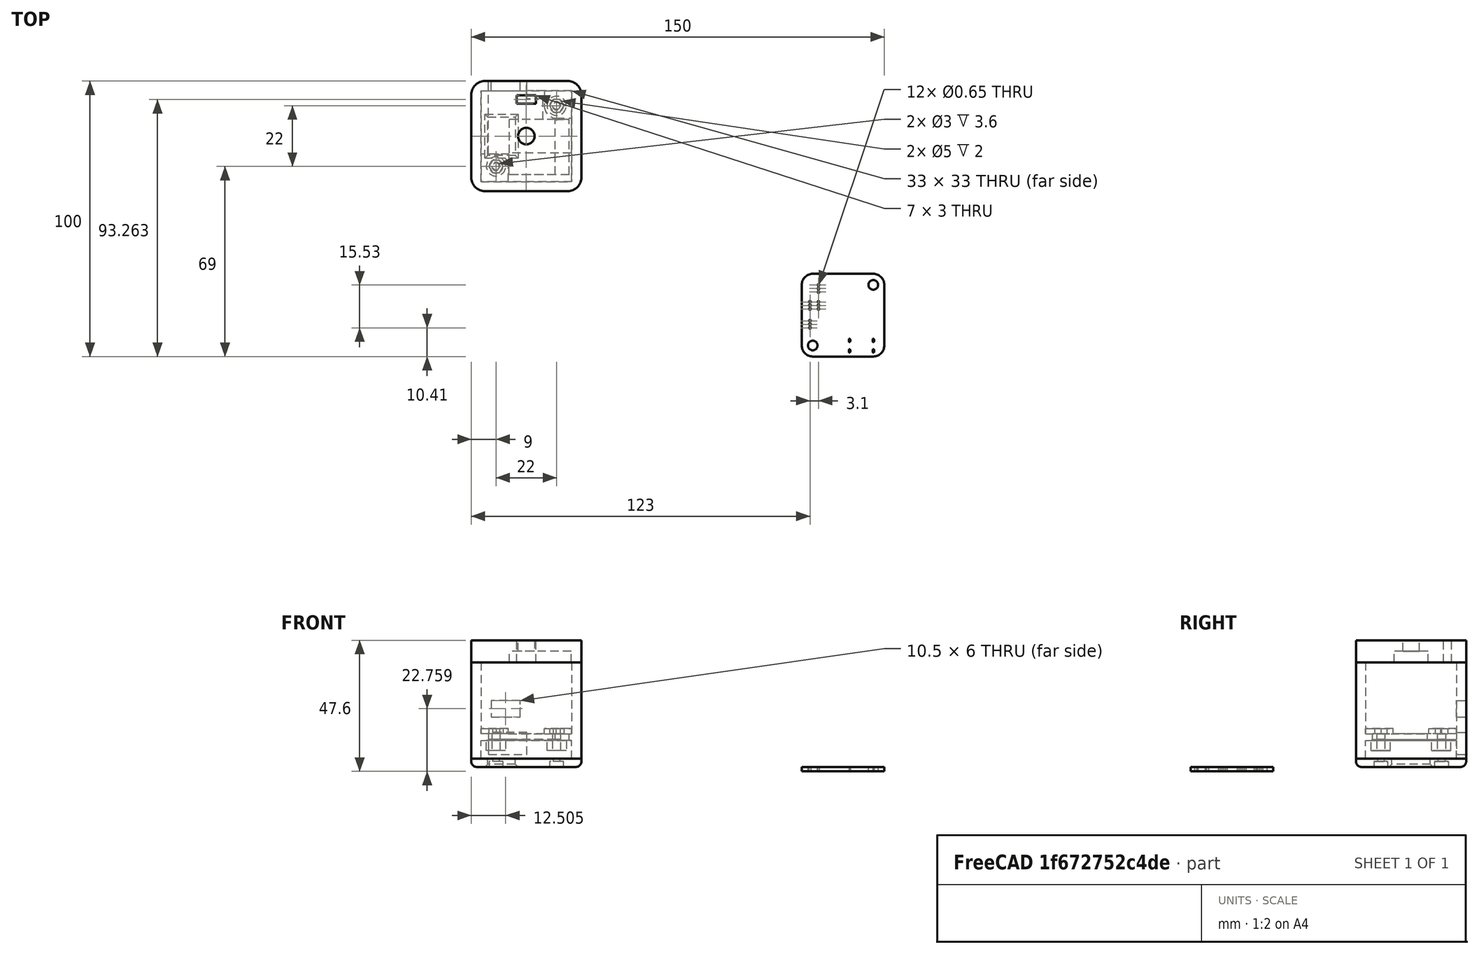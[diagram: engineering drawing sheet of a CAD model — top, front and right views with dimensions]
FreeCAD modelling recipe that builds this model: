
FCSTD DOCUMENT  (FreeCAD 1.0R39319 (Git))
Label: model
License: All rights reserved
LicenseURL: https://en.wikipedia.org/wiki/All_rights_reserved
objects: Sketcher::SketchObject×20, PartDesign::Pocket×13, PartDesign::Pad×6, PartDesign::Fillet×4, PartDesign::Body×3, App::Part×3, PartDesign::Chamfer×1, Mesh::Feature×1, PartDesign::CoordinateSystem×1, Part::Feature×1
note: 117 computed .brp shape members not serialized (recipe doc carries the construction recipe); baked Part::Feature solids carry a one-line shape summary decoded from their .brp

FEATURE [Sketcher::SketchObject] Sketch
  ArcFitTolerance = 1e-06
  AttachmentSupport = -> [XY_Plane]
  FullyConstrained = true
  MakeInternals = false
  MapMode = 5
  sketch-geometry (5):
    g0: LineSegment StartX=-20 StartY=-20 StartZ=0 EndX=20 EndY=-20 EndZ=0
    g1: LineSegment StartX=20 StartY=-20 StartZ=0 EndX=20 EndY=20 EndZ=0
    g2: LineSegment StartX=20 StartY=20 StartZ=0 EndX=-20 EndY=20 EndZ=0
    g3: LineSegment StartX=-20 StartY=20 StartZ=0 EndX=-20 EndY=-20 EndZ=0
    g4: GeomPoint [constr] X=0 Y=0 Z=0
  constraints (12):
    c: Coincident(g0,g1)
    c: Coincident(g1,g2)
    c: Coincident(g2,g3)
    c: Coincident(g3,g0)
    c: Horizontal(g0)
    c: Horizontal(g2)
    c: Vertical(g1)
    c: Vertical(g3)
    c: Symmetric(g2,g0,g4)
    c: Distance(g1,g3) = 40
    c: Distance(g0,g2) = 40
    c: Coincident(g4,g-1)
FEATURE [PartDesign::Pad] Pad
  Direction = (0,0,1)
  Length = 3
  Length2 = 10
  Profile = -> Sketch
  ReferenceAxis = -> Sketch [N_Axis]
  Refine = true
  Suppressed = false
  Type = 0
FEATURE [Sketcher::SketchObject] Sketch001
  ArcFitTolerance = 1e-06
  AttachmentSupport = -> [Pad]
  FullyConstrained = true
  MakeInternals = false
  MapMode = 5
  Placement = pos=(0,0,0) rot=(1,0,0;3.14159rad)
  sketch-geometry (2):
    g0: Circle CenterX=-11 CenterY=11 CenterZ=0 NormalX=0 NormalY=0 NormalZ=1 AngleXU=0 Radius=2.5
    g1: Circle CenterX=11 CenterY=-11 CenterZ=0 NormalX=0 NormalY=0 NormalZ=1 AngleXU=0 Radius=2.5
  constraints (6):
    c: Diameter(g0) = 5
    c: DistanceX(g0,g-1) = 11
    c: DistanceX(g0,g1) = 22
    c: Equal(g0,g1)
    c: DistanceY(g-1,g0) = 11
    c: DistanceY(g1,g0) = 22
FEATURE [PartDesign::Pocket] Pocket
  BaseFeature = -> Pad
  Direction = (0,0,1)
  Length = 2
  Length2 = 5
  Profile = -> Sketch001
  ReferenceAxis = -> Sketch001 [N_Axis]
  Refine = true
  Suppressed = false
  Type = 0
FEATURE [Sketcher::SketchObject] Sketch002
  ArcFitTolerance = 1e-06
  AttachmentSupport = -> [Pocket]
  ExternalGeometry = -> [Pocket]
  FullyConstrained = true
  MakeInternals = false
  MapMode = 5
  Placement = pos=(0,0,2) rot=(1,0,0;3.14159rad)
  sketch-geometry (2):
    g0: Circle CenterX=-11 CenterY=11 CenterZ=0 NormalX=0 NormalY=0 NormalZ=1 AngleXU=0 Radius=1.25
    g1: Circle CenterX=11 CenterY=-11 CenterZ=0 NormalX=0 NormalY=0 NormalZ=1 AngleXU=0 Radius=1.25
  constraints (4):
    c: Diameter(g0) = 2.5
    c: Coincident(g0,g-3)
    c: Diameter(g1) = 2.5
    c: Coincident(g1,g-4)
FEATURE [PartDesign::Pocket] Pocket001
  BaseFeature = -> Pocket
  Direction = (0,0,1)
  Length = 1
  Length2 = 5
  Profile = -> Sketch002
  ReferenceAxis = -> Sketch002 [N_Axis]
  Refine = true
  Suppressed = false
  Type = 0
FEATURE [PartDesign::Fillet] Fillet
  Base = -> Pocket001 [Edge1,Edge5,Edge8,Edge2]
  BaseFeature = -> Pocket001
  Radius = 5
  Refine = true
  SupportTransform = false
  Suppressed = false
  UseAllEdges = false
FEATURE [Sketcher::SketchObject] Sketch003
  ArcFitTolerance = 1e-06
  AttachmentSupport = -> [Fillet]
  ExternalGeometry = -> [Fillet]
  FullyConstrained = true
  MakeInternals = false
  MapMode = 5
  Placement = pos=(0,0,0) rot=(1,0,0;3.14159rad)
  sketch-geometry (9):
    g0: LineSegment StartX=-14 StartY=7 StartZ=0 EndX=-14 EndY=-7 EndZ=0
    g1: LineSegment StartX=-14 StartY=-7 StartZ=0 EndX=-4 EndY=-7 EndZ=0
    g2: LineSegment StartX=-4 StartY=-7 StartZ=0 EndX=-4 EndY=7 EndZ=0
    g3: LineSegment StartX=-4 StartY=7 StartZ=0 EndX=-14 EndY=7 EndZ=0
    g4: LineSegment [constr] StartX=-15 StartY=-15 StartZ=0 EndX=15 EndY=-15 EndZ=0
    g5: LineSegment [constr] StartX=15 StartY=-15 StartZ=0 EndX=15 EndY=15 EndZ=0
    g6: LineSegment [constr] StartX=15 StartY=15 StartZ=0 EndX=-15 EndY=15 EndZ=0
    g7: LineSegment [constr] StartX=-15 StartY=15 StartZ=0 EndX=-15 EndY=-15 EndZ=0
    g8: GeomPoint [constr] X=0 Y=0 Z=0
  constraints (24):
    c: Coincident(g0,g1)
    c: Coincident(g1,g2)
    c: Coincident(g2,g3)
    c: Coincident(g3,g0)
    c: Vertical(g0)
    c: Vertical(g2)
    c: Horizontal(g1)
    c: Horizontal(g3)
    c: Distance(g0,g2) = 10
    c: Distance(g1,g3) = 14
    c: Coincident(g4,g5)
    c: Coincident(g5,g6)
    c: Coincident(g6,g7)
    c: Coincident(g7,g4)
    c: Horizontal(g4)
    c: Horizontal(g6)
    c: Vertical(g5)
    c: Vertical(g7)
    c: Symmetric(g6,g4,g8)
    c: Distance(g5,g7) = 30
    c: Distance(g4,g6) = 30
    c: Coincident(g8,g-1)
    c: DistanceX(g4,g0) = 1
    c: DistanceY(g4,g0) = 8
FEATURE [PartDesign::Pocket] Pocket002
  BaseFeature = -> Fillet
  Direction = (0,0,1)
  Length = 3
  Length2 = 5
  Profile = -> Sketch003
  ReferenceAxis = -> Sketch003 [N_Axis]
  Refine = true
  Suppressed = false
  Type = 0
FEATURE [PartDesign::Chamfer] Chamfer
  Angle = 45
  Base = -> Pocket002 [Edge13,Edge16,Edge15,Edge14]
  BaseFeature = -> Pocket002
  ChamferType = 0
  FlipDirection = false
  Refine = true
  Size = 1
  Size2 = 1
  SupportTransform = false
  Suppressed = false
  UseAllEdges = false
FEATURE [Sketcher::SketchObject] Sketch004
  ArcFitTolerance = 1e-06
  AttachmentSupport = -> [XY_Plane001]
  FullyConstrained = true
  MakeInternals = false
  MapMode = 5
  sketch-geometry (5):
    g0: LineSegment StartX=-20 StartY=-20 StartZ=0 EndX=20 EndY=-20 EndZ=0
    g1: LineSegment StartX=20 StartY=-20 StartZ=0 EndX=20 EndY=20 EndZ=0
    g2: LineSegment StartX=20 StartY=20 StartZ=0 EndX=-20 EndY=20 EndZ=0
    g3: LineSegment StartX=-20 StartY=20 StartZ=0 EndX=-20 EndY=-20 EndZ=0
    g4: GeomPoint [constr] X=0 Y=0 Z=0
  constraints (12):
    c: Coincident(g0,g1)
    c: Coincident(g1,g2)
    c: Coincident(g2,g3)
    c: Coincident(g3,g0)
    c: Horizontal(g0)
    c: Horizontal(g2)
    c: Vertical(g1)
    c: Vertical(g3)
    c: Symmetric(g2,g0,g4)
    c: Distance(g1,g3) = 40
    c: Distance(g0,g2) = 40
    c: Coincident(g4,g-1)
FEATURE [PartDesign::Pad] Pad001  label="box"
  Direction = (0,0,1)
  Length = 35
  Length2 = 10
  Profile = -> Sketch004
  ReferenceAxis = -> Sketch004 [N_Axis]
  Refine = true
  Suppressed = false
  Type = 0
FEATURE [PartDesign::Fillet] Fillet001  label="rounded box"
  Base = -> Pad001 [Edge1,Edge2,Edge5,Edge8]
  BaseFeature = -> Pad001
  Radius = 5
  Refine = true
  SupportTransform = false
  Suppressed = false
  UseAllEdges = false
FEATURE [Sketcher::SketchObject] Sketch005
  ArcFitTolerance = 1e-06
  AttachmentSupport = -> [Fillet001]
  FullyConstrained = true
  MakeInternals = false
  MapMode = 5
  Placement = pos=(0,0,0) rot=(1,0,0;3.14159rad)
  sketch-geometry (5):
    g0: LineSegment StartX=-16.5 StartY=-16.5 StartZ=0 EndX=16.5 EndY=-16.5 EndZ=0
    g1: LineSegment StartX=16.5 StartY=-16.5 StartZ=0 EndX=16.5 EndY=16.5 EndZ=0
    g2: LineSegment StartX=16.5 StartY=16.5 StartZ=0 EndX=-16.5 EndY=16.5 EndZ=0
    g3: LineSegment StartX=-16.5 StartY=16.5 StartZ=0 EndX=-16.5 EndY=-16.5 EndZ=0
    g4: GeomPoint [constr] X=0 Y=0 Z=0
  constraints (12):
    c: Coincident(g0,g1)
    c: Coincident(g1,g2)
    c: Coincident(g2,g3)
    c: Coincident(g3,g0)
    c: Horizontal(g0)
    c: Horizontal(g2)
    c: Vertical(g1)
    c: Vertical(g3)
    c: Symmetric(g2,g0,g4)
    c: Distance(g1,g3) = 33
    c: Distance(g0,g2) = 33
    c: Coincident(g4,g-1)
FEATURE [PartDesign::Pocket] Pocket003  label="bottom hole"
  BaseFeature = -> Fillet001
  Direction = (0,0,1)
  Length = 7
  Length2 = 5
  Profile = -> Sketch005
  ReferenceAxis = -> Sketch005 [N_Axis]
  Refine = true
  Suppressed = false
  Type = 0
FEATURE [Sketcher::SketchObject] Sketch006
  ArcFitTolerance = 1e-06
  AttachmentSupport = -> [Pocket003]
  ExternalGeometry = -> [Pocket003]
  FullyConstrained = true
  MakeInternals = false
  MapMode = 5
  Placement = pos=(0,0,7) rot=(1,0,0;3.14159rad)
  sketch-geometry (4):
    g0: LineSegment StartX=15.5 StartY=14 StartZ=0 EndX=10.5 EndY=14 EndZ=0
    g1: LineSegment StartX=10.5 StartY=14 StartZ=0 EndX=10.5 EndY=-6 EndZ=0
    g2: LineSegment StartX=10.5 StartY=-6 StartZ=0 EndX=15.5 EndY=-6 EndZ=0
    g3: LineSegment StartX=15.5 StartY=-6 StartZ=0 EndX=15.5 EndY=14 EndZ=0
  constraints (12):
    c: Coincident(g0,g1)
    c: Coincident(g1,g2)
    c: Coincident(g2,g3)
    c: Coincident(g3,g0)
    c: Horizontal(g0)
    c: Horizontal(g2)
    c: Vertical(g1)
    c: Vertical(g3)
    c: Distance(g1,g3) = 5
    c: Distance(g0,g2) = 20
    c: DistanceX(g0,g-3) = 1
    c: DistanceY(g0,g-3) = 2.5
FEATURE [PartDesign::Pocket] Pocket004  label="cable hole"
  BaseFeature = -> Pocket003
  Direction = (0,0,1)
  Length = 2
  Length2 = 5
  Profile = -> Sketch006
  ReferenceAxis = -> Sketch006 [N_Axis]
  Refine = true
  Suppressed = false
  Type = 0
FEATURE [Sketcher::SketchObject] Sketch007
  ArcFitTolerance = 1e-06
  AttachmentSupport = -> [Pocket004]
  FullyConstrained = true
  MakeInternals = false
  MapMode = 5
  Placement = pos=(0,0,7) rot=(1,0,0;3.14159rad)
  sketch-geometry (2):
    g0: Circle CenterX=-11 CenterY=11 CenterZ=0 NormalX=0 NormalY=0 NormalZ=1 AngleXU=0 Radius=3.5
    g1: Circle CenterX=11 CenterY=-11 CenterZ=0 NormalX=0 NormalY=0 NormalZ=1 AngleXU=0 Radius=3.5
  constraints (6):
    c: Diameter(g0) = 7
    c: Diameter(g1) = 7
    c: DistanceX(g0,g1) = 22
    c: DistanceY(g1,g0) = 22
    c: DistanceY(g-1,g0) = 11
    c: DistanceX(g0,g-1) = 11
FEATURE [PartDesign::Pad] Pad002  label="standoffs"
  BaseFeature = -> Pocket004
  Direction = (0,0,-1)
  Length = 4
  Length2 = 10
  Profile = -> Sketch007
  ReferenceAxis = -> Sketch007 [N_Axis]
  Refine = true
  Suppressed = false
  Type = 0
FEATURE [Sketcher::SketchObject] Sketch009
  ArcFitTolerance = 1e-06
  FullyConstrained = true
  MakeInternals = false
  MapMode = 5
  Placement = pos=(0,0,40) rot=(0,0,1;0rad)
  sketch-geometry (5):
    g0: LineSegment StartX=-16.5 StartY=-16.5 StartZ=0 EndX=16.5 EndY=-16.5 EndZ=0
    g1: LineSegment StartX=16.5 StartY=-16.5 StartZ=0 EndX=16.5 EndY=16.5 EndZ=0
    g2: LineSegment StartX=16.5 StartY=16.5 StartZ=0 EndX=-16.5 EndY=16.5 EndZ=0
    g3: LineSegment StartX=-16.5 StartY=16.5 StartZ=0 EndX=-16.5 EndY=-16.5 EndZ=0
    g4: GeomPoint [constr] X=0 Y=0 Z=0
  constraints (12):
    c: Coincident(g0,g1)
    c: Coincident(g1,g2)
    c: Coincident(g2,g3)
    c: Coincident(g3,g0)
    c: Horizontal(g0)
    c: Horizontal(g2)
    c: Vertical(g1)
    c: Vertical(g3)
    c: Symmetric(g2,g0,g4)
    c: Distance(g1,g3) = 33
    c: Distance(g0,g2) = 33
    c: Coincident(g4,g-1)
FEATURE [PartDesign::Pocket] Pocket006  label="top hole"
  BaseFeature = -> Pad002
  Direction = (0,0,-1)
  Length = 31
  Length2 = 5
  Profile = -> Sketch009
  ReferenceAxis = -> Sketch009 [N_Axis]
  Refine = true
  Suppressed = false
  Type = 0
FEATURE [Sketcher::SketchObject] Sketch010
  ArcFitTolerance = 1e-06
  AttachmentSupport = -> [Pocket006]
  ExternalGeometry = -> [Pocket006]
  FullyConstrained = true
  MakeInternals = false
  MapMode = 5
  Placement = pos=(0,16.5,0) rot=(1,0,0;1.5708rad)
  sketch-geometry (4):
    g0: LineSegment StartX=-13.75 StartY=9.5 StartZ=0 EndX=-13.75 EndY=1.5 EndZ=0
    g1: LineSegment StartX=-13.75 StartY=1.5 StartZ=0 EndX=0.25 EndY=1.5 EndZ=0
    g2: LineSegment StartX=0.25 StartY=1.5 StartZ=0 EndX=0.25 EndY=9.5 EndZ=0
    g3: LineSegment StartX=0.25 StartY=9.5 StartZ=0 EndX=-13.75 EndY=9.5 EndZ=0
  constraints (12):
    c: Coincident(g0,g1)
    c: Coincident(g1,g2)
    c: Coincident(g2,g3)
    c: Coincident(g3,g0)
    c: Vertical(g0)
    c: Vertical(g2)
    c: Horizontal(g1)
    c: Horizontal(g3)
    c: DistanceX(g-3,g0) = 2.75
    c: DistanceX(g3,g3) = 14
    c: DistanceY(g0,g0) = 8
    c: DistanceY(g-3,g0) = 1.5
FEATURE [PartDesign::Pocket] Pocket007  label="usb hole"
  BaseFeature = -> Pocket006
  Direction = (0,1,-2e-16)
  Length = 4
  Length2 = 5
  Profile = -> Sketch010
  ReferenceAxis = -> Sketch010 [N_Axis]
  Refine = true
  Suppressed = false
  Type = 0
FEATURE [Sketcher::SketchObject] Sketch011
  ArcFitTolerance = 1e-06
  AttachmentSupport = -> [Pocket007]
  FullyConstrained = false
  MakeInternals = false
  MapMode = 5
  Placement = pos=(0,16.5,0) rot=(1,0,0;1.5708rad)
  sketch-geometry (4):
    g0: LineSegment StartX=-2.24469 StartY=15.159 StartZ=0 EndX=-2.24469 EndY=21.159 EndZ=0
    g1: LineSegment StartX=-2.24469 StartY=21.159 StartZ=0 EndX=-12.7447 EndY=21.159 EndZ=0
    g2: LineSegment StartX=-12.7447 StartY=21.159 StartZ=0 EndX=-12.7447 EndY=15.159 EndZ=0
    g3: LineSegment StartX=-12.7447 StartY=15.159 StartZ=0 EndX=-2.24469 EndY=15.159 EndZ=0
  constraints (10):
    c: Coincident(g0,g1)
    c: Coincident(g1,g2)
    c: Coincident(g2,g3)
    c: Coincident(g3,g0)
    c: Vertical(g0)
    c: Vertical(g2)
    c: Horizontal(g1)
    c: Horizontal(g3)
    c: DistanceX(g1,g1) = 10.5
    c: DistanceY(g2,g2) = 6
FEATURE [PartDesign::Pocket] Pocket008  label="dmx hole"
  BaseFeature = -> Pocket007
  Direction = (0,1,-2e-16)
  Length = 4
  Length2 = 5
  Profile = -> Sketch011
  ReferenceAxis = -> Sketch011 [N_Axis]
  Refine = true
  Suppressed = false
  Type = 0
FEATURE [Sketcher::SketchObject] Sketch012
  ArcFitTolerance = 1e-06
  AttachmentSupport = -> [Pocket008]
  ExternalGeometry = -> [Pocket008]
  FullyConstrained = false
  MakeInternals = false
  MapMode = 5
  Placement = pos=(0,0,9) rot=(0,0,1;0rad)
  sketch-geometry (10):
    g0: LineSegment StartX=16.5 StartY=16.5 StartZ=0 EndX=6.5 EndY=16.5 EndZ=0
    g1: LineSegment StartX=6.5 StartY=16.5 StartZ=0 EndX=6.5 EndY=10.8083 EndZ=0
    g2: LineSegment StartX=10.8083 StartY=6.5 StartZ=0 EndX=16.5 EndY=6.5 EndZ=0
    g3: LineSegment StartX=16.5 StartY=6.5 StartZ=0 EndX=16.5 EndY=16.5 EndZ=0
    g4: LineSegment StartX=-16.5 StartY=-16.5 StartZ=0 EndX=-6.5 EndY=-16.5 EndZ=0
    g5: LineSegment StartX=-6.5 StartY=-16.5 StartZ=0 EndX=-6.5 EndY=-10.8083 EndZ=0
    g6: LineSegment StartX=-10.8083 StartY=-6.5 StartZ=0 EndX=-16.5 EndY=-6.5 EndZ=0
    g7: LineSegment StartX=-16.5 StartY=-6.5 StartZ=0 EndX=-16.5 EndY=-16.5 EndZ=0
    g8: ArcOfCircle CenterX=11 CenterY=11 CenterZ=0 NormalX=0 NormalY=0 NormalZ=1 AngleXU=0 Radius=4.50408 StartAngle=3.18416 EndAngle=4.66982
    g9: ArcOfCircle CenterX=-11 CenterY=-11 CenterZ=0 NormalX=0 NormalY=0 NormalZ=1 AngleXU=0 Radius=4.50408 StartAngle=0.0425652 EndAngle=1.52823
  constraints (27):
    c: Coincident(g0,g1)
    c: Coincident(g2,g3)
    c: Coincident(g3,g0)
    c: Horizontal(g0)
    c: Horizontal(g2)
    c: Vertical(g1)
    c: Vertical(g3)
    c: Coincident(g0,g-8)
    c: Coincident(g4,g5)
    c: Coincident(g6,g7)
    c: Coincident(g7,g4)
    c: Horizontal(g4)
    c: Horizontal(g6)
    c: Vertical(g5)
    c: Vertical(g7)
    c: Coincident(g4,g-7)
    c: Equal(g4,g7)
    c: Equal(g7,g0)
    c: Equal(g0,g3)
    c: Equal(g5,g2)
    c: Coincident(g8,g-4)
    c: Coincident(g8,g2)
    c: Coincident(g8,g1)
    c: Coincident(g9,g-3)
    c: Coincident(g9,g6)
    c: Coincident(g9,g5)
    c: DistanceY(g3,g3) = 10
FEATURE [PartDesign::Pad] Pad003
  BaseFeature = -> Pocket008
  Direction = (0,0,1)
  Length = 2
  Length2 = 10
  Profile = -> Sketch012
  ReferenceAxis = -> Sketch012 [N_Axis]
  Refine = true
  Suppressed = false
  Type = 0
FEATURE [Sketcher::SketchObject] Sketch013
  ArcFitTolerance = 1e-06
  AttachmentSupport = -> [Pad003]
  ExternalGeometry = -> [Pad003]
  FullyConstrained = true
  MakeInternals = false
  MapMode = 5
  Placement = pos=(0,0,3) rot=(1,0,0;3.14159rad)
  sketch-geometry (2):
    g0: Circle CenterX=-11 CenterY=11 CenterZ=0 NormalX=0 NormalY=0 NormalZ=1 AngleXU=0 Radius=1.5
    g1: Circle CenterX=11 CenterY=-11 CenterZ=0 NormalX=0 NormalY=0 NormalZ=1 AngleXU=0 Radius=1.5
  constraints (4):
    c: Diameter(g0) = 3
    c: Coincident(g0,g-4)
    c: Diameter(g1) = 3
    c: Coincident(g1,g-3)
FEATURE [PartDesign::Pocket] Pocket009
  BaseFeature = -> Pad003
  Direction = (0,0,1)
  Length = 8
  Length2 = 5
  Profile = -> Sketch013
  ReferenceAxis = -> Sketch013 [N_Axis]
  Refine = true
  Suppressed = false
  Type = 0
FEATURE [Sketcher::SketchObject] Sketch014
  ArcFitTolerance = 1e-06
  AttachmentSupport = -> [Pocket009]
  ExternalGeometry = -> [Pocket009]
  FullyConstrained = true
  MakeInternals = false
  MapMode = 5
  Placement = pos=(0,0,11) rot=(0,0,1;0rad)
  sketch-geometry (14):
    g0: LineSegment StartX=13.6 StartY=11 StartZ=0 EndX=12.3 EndY=13.2517 EndZ=0
    g1: LineSegment StartX=12.3 StartY=13.2517 StartZ=0 EndX=9.7 EndY=13.2517 EndZ=0
    g2: LineSegment StartX=9.7 StartY=13.2517 StartZ=0 EndX=8.4 EndY=11 EndZ=0
    g3: LineSegment StartX=8.4 StartY=11 StartZ=0 EndX=9.7 EndY=8.74833 EndZ=0
    g4: LineSegment StartX=9.7 StartY=8.74833 StartZ=0 EndX=12.3 EndY=8.74833 EndZ=0
    g5: LineSegment StartX=12.3 StartY=8.74833 StartZ=0 EndX=13.6 EndY=11 EndZ=0
    g6: Circle [constr] CenterX=11 CenterY=11 CenterZ=0 NormalX=0 NormalY=0 NormalZ=1 AngleXU=0 Radius=2.6
    g7: LineSegment StartX=-8.4 StartY=-11 StartZ=0 EndX=-9.7 EndY=-8.74833 EndZ=0
    g8: LineSegment StartX=-9.7 StartY=-8.74833 StartZ=0 EndX=-12.3 EndY=-8.74833 EndZ=0
    g9: LineSegment StartX=-12.3 StartY=-8.74833 StartZ=0 EndX=-13.6 EndY=-11 EndZ=0
    g10: LineSegment StartX=-13.6 StartY=-11 StartZ=0 EndX=-12.3 EndY=-13.2517 EndZ=0
    g11: LineSegment StartX=-12.3 StartY=-13.2517 StartZ=0 EndX=-9.7 EndY=-13.2517 EndZ=0
    g12: LineSegment StartX=-9.7 StartY=-13.2517 StartZ=0 EndX=-8.4 EndY=-11 EndZ=0
    g13: Circle [constr] CenterX=-11 CenterY=-11 CenterZ=0 NormalX=0 NormalY=0 NormalZ=1 AngleXU=0 Radius=2.6
  constraints (32):
    c: Coincident(g0,g1)
    c: Coincident(g1,g2)
    c: Coincident(g2,g3)
    c: Coincident(g3,g4)
    c: Coincident(g4,g5)
    c: Coincident(g5,g0)
    c: Equal(g0, g1-g5) x5
    c: PointOnObject(g0,g6)
    c: PointOnObject(g1,g6)
    c: PointOnObject(g2,g6)
    c: PointOnObject(g3,g6)
    c: PointOnObject(g4,g6)
    c: PointOnObject(g5,g6)
    c: Radius(g6) = 2.6
    c: Coincident(g6,g-3)
    c: Coincident(g7,g8)
    c: Coincident(g8,g9)
    c: Coincident(g9,g10)
    c: Coincident(g10,g11)
    c: Coincident(g11,g12)
    c: Coincident(g12,g7)
    c: Equal(g7, g8-g12) x5
    c: PointOnObject(g7,g13)
    c: PointOnObject(g8,g13)
    c: PointOnObject(g9,g13)
    c: PointOnObject(g10,g13)
    c: PointOnObject(g11,g13)
    c: PointOnObject(g12,g13)
    c: Radius(g13) = 2.6
    c: Coincident(g13,g-4)
    c: Horizontal(g8)
    c: Horizontal(g1)
FEATURE [PartDesign::Pocket] Pocket010
  BaseFeature = -> Pocket009
  Direction = (0,0,-1)
  Length = 2
  Length2 = 5
  Profile = -> Sketch014
  ReferenceAxis = -> Sketch014 [N_Axis]
  Refine = true
  Suppressed = false
  Type = 0
FEATURE [PartDesign::Fillet] Fillet002
  Base = -> Chamfer [Edge6,Edge8,Edge5,Edge7,Edge9,Edge11,Edge12,Edge10]
  BaseFeature = -> Chamfer
  Radius = 2
  Refine = true
  SupportTransform = false
  Suppressed = false
  UseAllEdges = false
FEATURE [PartDesign::Body] Body  label="bottom cover"
  AllowCompound = false
  Group = -> [Sketch,Pad,Sketch001,Pocket,Sketch002,Pocket001,Fillet,Sketch003,Pocket002,Chamfer,Fillet002]
  Origin = -> Origin
  Tip = -> Fillet002
FEATURE [Sketcher::SketchObject] Sketch015
  ArcFitTolerance = 1e-06
  AttachmentSupport = -> [Pocket010]
  ExternalGeometry = -> [Pocket010]
  FullyConstrained = true
  MakeInternals = false
  MapMode = 5
  Placement = pos=(0,0,7) rot=(1,0,0;3.14159rad)
  sketch-geometry (14):
    g0: LineSegment StartX=-16.5 StartY=16.5 StartZ=0 EndX=16.5 EndY=16.5 EndZ=0
    g1: LineSegment StartX=16.5 StartY=16.5 StartZ=0 EndX=16.5 EndY=-16.5 EndZ=0
    g2: LineSegment StartX=16.5 StartY=-16.5 StartZ=0 EndX=0.25 EndY=-16.5 EndZ=0
    g3: LineSegment StartX=-16.5 StartY=16.5 StartZ=0 EndX=-16.5 EndY=-16.5 EndZ=0
    g4: LineSegment StartX=-16.5 StartY=-16.5 StartZ=0 EndX=-13.75 EndY=-16.5 EndZ=0
    g5: LineSegment StartX=15.5 StartY=14 StartZ=0 EndX=15.5 EndY=-6 EndZ=0
    g6: LineSegment StartX=15.5 StartY=-6 StartZ=0 EndX=6 EndY=-6 EndZ=0
    g7: LineSegment StartX=15.5 StartY=14 StartZ=0 EndX=-6.25 EndY=14 EndZ=0
    g8: LineSegment StartX=-6.25 StartY=14 StartZ=0 EndX=-6.25 EndY=6.5 EndZ=0
    g9: LineSegment StartX=-6.25 StartY=6.5 StartZ=0 EndX=-13.75 EndY=6.5 EndZ=0
    g10: LineSegment StartX=-13.75 StartY=6.5 StartZ=0 EndX=-13.75 EndY=-16.5 EndZ=0
    g11: LineSegment StartX=6 StartY=-6 StartZ=0 EndX=6 EndY=-13.5 EndZ=0
    g12: LineSegment StartX=6 StartY=-13.5 StartZ=0 EndX=0.25 EndY=-13.5 EndZ=0
    g13: LineSegment StartX=0.25 StartY=-13.5 StartZ=0 EndX=0.25 EndY=-16.5 EndZ=0
  constraints (34):
    c: Coincident(g0,g-5)
    c: Coincident(g0,g-5)
    c: Coincident(g1,g0)
    c: Coincident(g1,g-3)
    c: Coincident(g2,g1)
    c: Coincident(g2,g-3)
    c: Coincident(g3,g0)
    c: Coincident(g3,g-4)
    c: Coincident(g4,g3)
    c: Coincident(g4,g-6)
    c: Coincident(g6,g5)
    c: Horizontal(g6)
    c: Coincident(g5,g-7)
    c: Coincident(g7,g5)
    c: Horizontal(g7)
    c: Coincident(g8,g7)
    c: Vertical(g8)
    c: Coincident(g9,g8)
    c: Horizontal(g9)
    c: Coincident(g10,g9)
    c: Coincident(g10,g4)
    c: Vertical(g10)
    c: DistanceY(g8,g8) = 7.5
    c: DistanceX(g9,g9) = 7.5
    c: Coincident(g5,g-7)
    c: DistanceX(g6,g6) = 9.5
    c: Coincident(g11,g6)
    c: Vertical(g11)
    c: Coincident(g12,g11)
    c: Horizontal(g12)
    c: Coincident(g13,g12)
    c: Coincident(g13,g2)
    c: Vertical(g13)
    c: DistanceY(g11,g11) = 7.5
FEATURE [PartDesign::Pad] Pad004
  BaseFeature = -> Pocket010
  Direction = (0,0,-1)
  Length = 0.4
  Length2 = 10
  Profile = -> Sketch015
  ReferenceAxis = -> Sketch015 [N_Axis]
  Refine = true
  Suppressed = false
  Type = 0
FEATURE [PartDesign::Body] Body001  label="base"
  AllowCompound = false
  Group = -> [Sketch004,Pad001,Fillet001,Sketch005,Pocket003,Sketch006,Pocket004,Sketch007,Pad002,Sketch009,Pocket006,Sketch010,Pocket007,Sketch011,Pocket008,Sketch012,Pad003,Sketch013,Pocket009,Sketch014,Pocket010,Sketch015,Pad004]
  Origin = -> Origin001
  Placement = pos=(0,0,3) rot=(0,0,1;0rad)
  Tip = -> Pad004
FEATURE [Mesh::Feature] _g_servo  label="9g_servo"
  Placement = pos=(5,6,30) rot=(1,0,0;1.5708rad)
FEATURE [PartDesign::CoordinateSystem] Local_CS_8e13
  AttacherType = Attacher::AttachEngine3D
  MapMode = 2
  Placement = pos=(115,-65,0) rot=(0,0,1;0rad)
FEATURE [Sketcher::SketchObject] PCB_Sketch_8e13
  ArcFitTolerance = 1e-06
  FullyConstrained = false
  MakeInternals = false
  sketch-geometry (8):
    g0: LineSegment StartX=104 StartY=-50 StartZ=0 EndX=126 EndY=-50 EndZ=0
    g1: LineSegment StartX=100 StartY=-76 StartZ=0 EndX=100 EndY=-54 EndZ=0
    g2: LineSegment StartX=126 StartY=-80 StartZ=0 EndX=104 EndY=-80 EndZ=0
    g3: LineSegment StartX=130 StartY=-54 StartZ=0 EndX=130 EndY=-76 EndZ=0
    g4: ArcOfCircle CenterX=126 CenterY=-76 CenterZ=0 NormalX=0 NormalY=0 NormalZ=-1 AngleXU=-3.14159 Radius=4 StartAngle=0 EndAngle=1.5708
    g5: ArcOfCircle CenterX=104 CenterY=-76 CenterZ=0 NormalX=0 NormalY=0 NormalZ=-1 AngleXU=-1.5708 Radius=4 StartAngle=0 EndAngle=1.5708
    g6: ArcOfCircle CenterX=104 CenterY=-54 CenterZ=0 NormalX=0 NormalY=0 NormalZ=-1 AngleXU=1.06478e-07 Radius=4 StartAngle=0 EndAngle=1.5708
    g7: ArcOfCircle CenterX=126 CenterY=-54 CenterZ=0 NormalX=0 NormalY=0 NormalZ=-1 AngleXU=1.5708 Radius=4 StartAngle=0 EndAngle=1.5708
  constraints (8):
    c: Coincident(g1,g5)
    c: Coincident(g1,g6)
    c: Coincident(g2,g5)
    c: Coincident(g0,g6)
    c: Coincident(g2,g4)
    c: Coincident(g0,g7)
    c: Coincident(g3,g4)
    c: Coincident(g3,g7)
FEATURE [Part::Feature] Pcb_8e13
  shape: bbox 30 x 30 x 1.6 mm, 48 faces (baked)
FEATURE [App::Part] Board_Geoms_8e13
  Group = -> [Pcb_8e13,PCB_Sketch_8e13]
  Origin = -> Origin002
FEATURE [App::Part] Step_Models_8e13
  Origin = -> Origin004
FEATURE [App::Part] Board_8e13  label="desk-mh"
  Group = -> [Local_CS_8e13,Board_Geoms_8e13,Step_Models_8e13]
  Origin = -> Origin003
  Placement = pos=(115,-65,6) rot=(0,0,1;3.14159rad)
FEATURE [Sketcher::SketchObject] Sketch016
  ArcFitTolerance = 1e-06
  AttachmentSupport = -> [XY_Plane005]
  FullyConstrained = true
  MakeInternals = false
  MapMode = 5
  sketch-geometry (5):
    g0: LineSegment StartX=-20 StartY=-20 StartZ=0 EndX=20 EndY=-20 EndZ=0
    g1: LineSegment StartX=20 StartY=-20 StartZ=0 EndX=20 EndY=20 EndZ=0
    g2: LineSegment StartX=20 StartY=20 StartZ=0 EndX=-20 EndY=20 EndZ=0
    g3: LineSegment StartX=-20 StartY=20 StartZ=0 EndX=-20 EndY=-20 EndZ=0
    g4: GeomPoint [constr] X=0 Y=0 Z=0
  constraints (12):
    c: Coincident(g0,g1)
    c: Coincident(g1,g2)
    c: Coincident(g2,g3)
    c: Coincident(g3,g0)
    c: Horizontal(g0)
    c: Horizontal(g2)
    c: Vertical(g1)
    c: Vertical(g3)
    c: Symmetric(g2,g0,g4)
    c: Distance(g1,g3) = 40
    c: Distance(g0,g2) = 40
    c: Coincident(g4,g-1)
FEATURE [PartDesign::Pad] Pad005
  Direction = (0,0,1)
  Length = 8
  Length2 = 10
  Profile = -> Sketch016
  ReferenceAxis = -> Sketch016 [N_Axis]
  Suppressed = false
  Type = 0
FEATURE [PartDesign::Fillet] Fillet003
  Base = -> Pad005 [Edge1,Edge2,Edge5,Edge8]
  BaseFeature = -> Pad005
  Radius = 5
  SupportTransform = false
  Suppressed = false
  UseAllEdges = false
FEATURE [Sketcher::SketchObject] Sketch017
  ArcFitTolerance = 1e-06
  AttachmentSupport = -> [Fillet003]
  FullyConstrained = true
  MakeInternals = false
  MapMode = 5
  Placement = pos=(0,0,0) rot=(1,0,0;3.14159rad)
  sketch-geometry (6):
    g0: LineSegment StartX=-6.2 StartY=6.15 StartZ=0 EndX=-6.2 EndY=-6.15 EndZ=0
    g1: LineSegment StartX=-6.2 StartY=-6.15 StartZ=0 EndX=16.3 EndY=-6.15 EndZ=0
    g2: LineSegment StartX=16.3 StartY=-6.15 StartZ=0 EndX=16.3 EndY=6.15 EndZ=0
    g3: LineSegment StartX=16.3 StartY=6.15 StartZ=0 EndX=-6.2 EndY=6.15 EndZ=0
    g4: LineSegment [constr] StartX=-6.2 StartY=6.15 StartZ=0 EndX=0 EndY=0 EndZ=0
    g5: LineSegment [constr] StartX=0 StartY=0 StartZ=0 EndX=-6.2 EndY=-6.15 EndZ=0
  constraints (16):
    c: Coincident(g0,g1)
    c: Coincident(g1,g2)
    c: Coincident(g2,g3)
    c: Coincident(g3,g0)
    c: Vertical(g0)
    c: Vertical(g2)
    c: Horizontal(g1)
    c: Horizontal(g3)
    c: Coincident(g4,g0)
    c: Coincident(g4,g-1)
    c: Coincident(g5,g4)
    c: Coincident(g5,g0)
    c: Equal(g5,g4)
    c: DistanceY(g2,g2) = 12.3
    c: DistanceX(g3,g3) = 22.5
    c: DistanceX(g0,g4) = 6.2
FEATURE [PartDesign::Pocket] Pocket011
  BaseFeature = -> Fillet003
  Direction = (0,0,1)
  Length = 4
  Length2 = 5
  Profile = -> Sketch017
  ReferenceAxis = -> Sketch017 [N_Axis]
  Suppressed = false
  Type = 0
FEATURE [Sketcher::SketchObject] Sketch018
  ArcFitTolerance = 1e-06
  AttachmentSupport = -> [Pocket011]
  FullyConstrained = true
  MakeInternals = false
  MapMode = 5
  Placement = pos=(0,0,8) rot=(0,0,1;0rad)
  sketch-geometry (1):
    g0: Circle CenterX=0 CenterY=0 CenterZ=0 NormalX=0 NormalY=0 NormalZ=1 AngleXU=0 Radius=3
  constraints (2):
    c: Coincident(g0,g-1)
    c: Diameter(g0) = 6
FEATURE [PartDesign::Pocket] Pocket012
  BaseFeature = -> Pocket011
  Direction = (0,0,-1)
  Length = 5
  Length2 = 5
  Profile = -> Sketch018
  ReferenceAxis = -> Sketch018 [N_Axis]
  Suppressed = false
  Type = 0
FEATURE [Sketcher::SketchObject] Sketch019
  ArcFitTolerance = 1e-06
  AttachmentSupport = -> [Pocket012]
  FullyConstrained = false
  MakeInternals = false
  MapMode = 5
  Placement = pos=(0,0,0) rot=(1,0,0;3.14159rad)
  sketch-geometry (5):
    g0: LineSegment StartX=-3.5 StartY=-14.7633 StartZ=0 EndX=3.5 EndY=-14.7633 EndZ=0
    g1: LineSegment StartX=3.5 StartY=-14.7633 StartZ=0 EndX=3.5 EndY=-11.7633 EndZ=0
    g2: LineSegment StartX=3.5 StartY=-11.7633 StartZ=0 EndX=-3.5 EndY=-11.7633 EndZ=0
    g3: LineSegment StartX=-3.5 StartY=-11.7633 StartZ=0 EndX=-3.5 EndY=-14.7633 EndZ=0
    g4: GeomPoint [constr] X=0 Y=-13.2633 Z=0
  constraints (12):
    c: Coincident(g0,g1)
    c: Coincident(g1,g2)
    c: Coincident(g2,g3)
    c: Coincident(g3,g0)
    c: Horizontal(g0)
    c: Horizontal(g2)
    c: Vertical(g1)
    c: Vertical(g3)
    c: Symmetric(g2,g0,g4)
    c: Distance(g1,g3) = 7
    c: Distance(g0,g2) = 3
    c: PointOnObject(g4,g-2)
FEATURE [PartDesign::Pocket] Pocket013
  BaseFeature = -> Pocket012
  Direction = (0,0,1)
  Length = 5
  Length2 = 5
  Profile = -> Sketch019
  ReferenceAxis = -> Sketch019 [N_Axis]
  Refine = true
  Suppressed = false
  Type = 2
FEATURE [PartDesign::Body] Body002  label="base cover"
  AllowCompound = false
  Group = -> [Sketch016,Pad005,Fillet003,Sketch017,Pocket011,Sketch018,Pocket012,Sketch019,Pocket013]
  Origin = -> Origin005
  Placement = pos=(0,0,38) rot=(0,0,1;0rad)
  Tip = -> Pocket013
